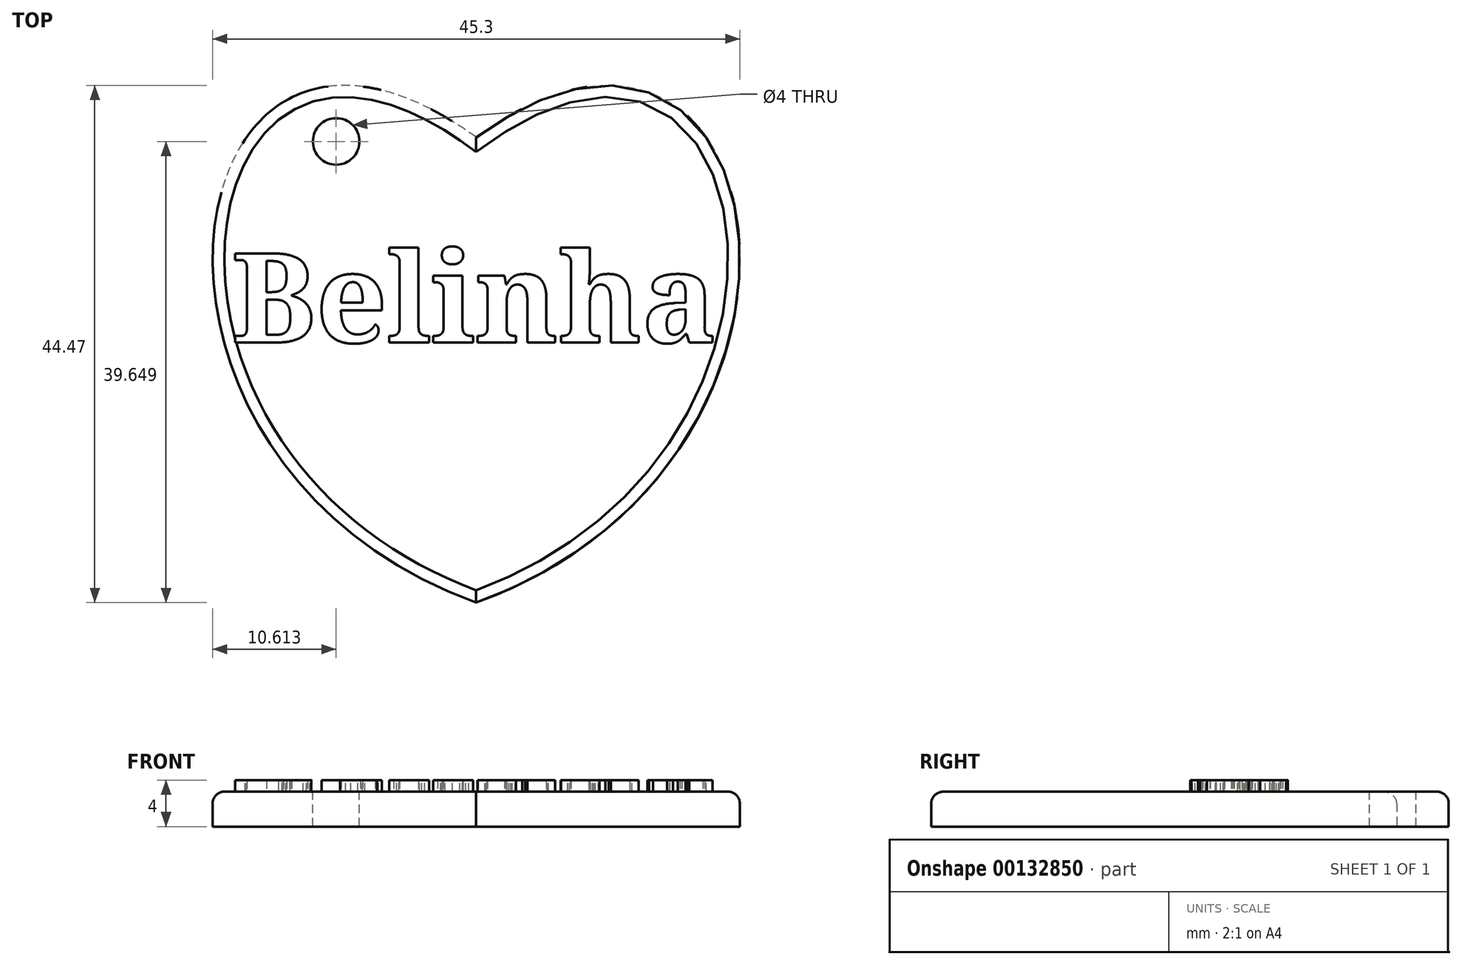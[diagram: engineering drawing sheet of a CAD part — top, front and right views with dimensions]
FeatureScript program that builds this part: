
annotation { "Feature Type Name" : "Feature", "Feature Type Description" : "" }
export const myFeature = defineFeature(function(context is Context, id is Id, definition is map)
    precondition{}
    {
        {
            var Q0;
            Q0=qCreatedBy(makeId("Top.planeOp"),FACE);
            var sketch = newSketch(context, id + "F0", { "sketchPlane" : qUnion([Q0])});
            skFitSpline(sketch, "E0", {"points": [v(0, 22) * mm, v(0, -18) * mm], "startDerivative": vector(77.88, 56.74) * mm, "endDerivative": vector(-102.46, -37.42) * mm});
            skLineSegment(sketch, "E1", {"start": v(0, 22) * mm, "end": v(0, -18) * mm, "construction": true});
            skFitSpline(sketch, "E2.MirrorCS", {"points": [v(0, 22) * mm, v(0, -18) * mm], "startDerivative": vector(-77.88, 56.74) * mm, "endDerivative": vector(102.46, -37.42) * mm});
            skSolve(sketch);
        }
        {
            var Q0;
            Q0=makeQuery(id+"F0.imprint","IMPRINT",FACE,{"disambiguationData":[TD([[makeQuery(id+"F0.imprint","IMPRINT",EDGE,{"derivedFrom":sQuery(id+"F0.wireOp",EDGE,"E0")}),-1.0]])]});
            extrude(context, id + "F1", {"entities" : qUnion([Q0]), "offsetDistance" : 25 * mm, "depth" : 3 * mm});
        }
        {
            var Q0;
            Q0=makeQuery(id+"F1.opExtrude","CAP_FACE",FACE,{"disambiguationData":[OSD([sQuery(id+"F0.wireOp",EDGE,"E0"),sQuery(id+"F0.wireOp",EDGE,"E2.MirrorCS")])],"isStart":false});
            var sketch = newSketch(context, id + "F2", { "sketchPlane" : qUnion([Q0])});
            skText(sketch, "E3", { "text": "Belinha", "fontName": "NotoSerif-Bold.ttf"});
            const initialGuessF2  = {"E3": [-0.021, 0.00436, 1, 0, 0.00773]};
            skSetInitialGuess(sketch, initialGuessF2);
            skSolve(sketch);
        }
        {
            var Q0;
            Q0 = qSketchRegion(id + "F2", true);
            extrude(context, id + "F3", {"entities" : qUnion([Q0]), "operationType" : NewBodyOperationType.ADD, "depth" : 1 * mm});
        }
        {
            var Q0;
            Q0=makeQuery(id+"F1.opExtrude","CAP_EDGE",EDGE,{"disambiguationData":[OSD([sQuery(id+"F0.wireOp",EDGE,"E0")])],"isStart":false});
            var Q1;
            Q1=makeQuery(id+"F1.opExtrude","CAP_EDGE",EDGE,{"disambiguationData":[OSD([sQuery(id+"F0.wireOp",EDGE,"E2.MirrorCS")])],"isStart":false});
            fillet(context, id + "F4", {"entities" : qUnion([Q0, Q1]), "radius" : 1 * mm, "tangentPropagation" : true, "allowEdgeOverflow" : false});
        }
        {
            var Q0;
            {var subQ0=sQuery(id+"F0.wireOp",EDGE,"E0");var subQ1=sQuery(id+"F0.wireOp",EDGE,"E2.MirrorCS");Q0=makeQuery(id+"F3.boolean.opBoolean","SPLIT",FACE,{"disambiguationData":[TD([makeQuery(id+"F1.opExtrude","SWEPT_FACE",FACE,{"disambiguationData":[OSD([subQ0])]})])],"derivedFrom":makeQuery(id+"F1.opExtrude","CAP_FACE",FACE,{"disambiguationData":[OSD([subQ0,subQ1])],"isStart":false})});}
            var sketch = newSketch(context, id + "F5", { "sketchPlane" : qUnion([Q0])});
            skCircle(sketch, "E4", {"center": v(-12.04, 21.65) * mm, "radius": 2 * mm});
            skSolve(sketch);
        }
        {
            var Q0;
            Q0 = qSketchRegion(id + "F5", true);
            extrude(context, id + "F6", {"entities" : qUnion([Q0]), "operationType" : NewBodyOperationType.REMOVE, "endBound" : BoundingType.THROUGH_ALL, "oppositeDirection" : true, "depth" : 25 * mm, "offsetDistance" : 25 * mm});
        }
    });
